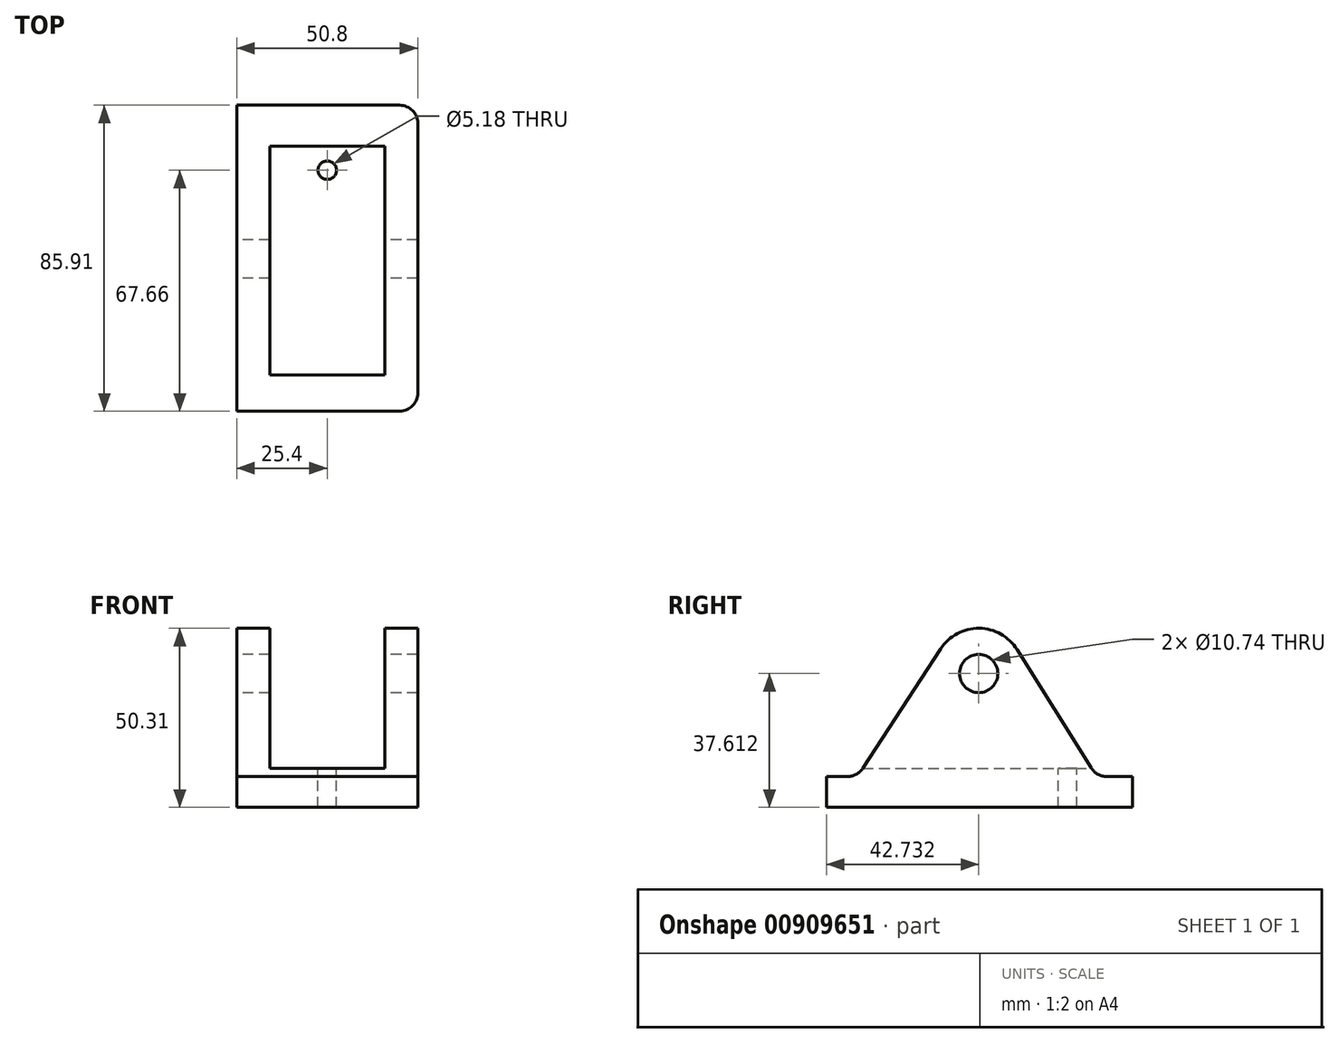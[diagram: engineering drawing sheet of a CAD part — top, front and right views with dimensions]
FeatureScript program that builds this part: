
annotation { "Feature Type Name" : "Feature", "Feature Type Description" : "" }
export const myFeature = defineFeature(function(context is Context, id is Id, definition is map)
    precondition{}
    {
        {
            var Q0;
            Q0=qCreatedBy(makeId("Right.planeOp"),FACE);
            var sketch = newSketch(context, id + "F0", { "sketchPlane" : qUnion([Q0])});
            skLineSegment(sketch, "E0.bottom", {"start": v(-40.85, -18.95) * mm, "end": v(45.06, -18.95) * mm});
            skLineSegment(sketch, "E0.top", {"start": v(-40.85, -27.65) * mm, "end": v(45.06, -27.65) * mm});
            skLineSegment(sketch, "E0.left", {"start": v(-40.85, -18.95) * mm, "end": v(-40.85, -27.65) * mm});
            skLineSegment(sketch, "E0.right", {"start": v(45.06, -18.95) * mm, "end": v(45.06, -27.65) * mm});
            skPoint(sketch, "E1.snap10", {"position": v(2.1, -18.95) * mm});
            skPoint(sketch, "E2.visualSharp", {"position": v(2.1, 33.55) * mm});
            skLineSegment(sketch, "E3", {"start": v(34.95, -18.95) * mm, "end": v(12.65, 16.7) * mm});
            skLineSegment(sketch, "E4", {"start": v(-8.75, 16.9) * mm, "end": v(-32.14, -18.95) * mm});
            skArc(sketch, "E5.filletArc", {"start": v(12.65, 16.7) * mm, "mid": v(2, 22.66) * mm, "end": v(-8.75, 16.9) * mm});
            skPoint(sketch, "E6", {"position": v(0, 0) * mm});
            skCircle(sketch, "E7", {"center": v(1.88, 9.96) * mm, "radius": 5.37 * mm});
            skSolve(sketch);
        }
        {
            var Q0;
            {var subQ0=sQuery(id+"F0.wireOp",EDGE,"E3");Q0=makeQuery(id+"F0.imprint","IMPRINT",FACE,{"disambiguationData":[TD([[makeQuery(id+"F0.imprint","IMPRINT",EDGE,{"derivedFrom":subQ0}),1.0]])]});}
            var Q1;
            Q1=makeQuery(id+"F0.imprint","IMPRINT",FACE,{"disambiguationData":[TD([[makeQuery(id+"F0.imprint","IMPRINT",EDGE,{"derivedFrom":sQuery(id+"F0.wireOp",EDGE,"E0.top")}),1.0]])]});
            extrude(context, id + "F1", {"entities" : qUnion([Q0, Q1]), "endBound" : BoundingType.SYMMETRIC, "depth" : 50.8 * mm, "offsetDistance" : 25.4 * mm});
        }
        {
            var Q0;
            Q0=makeQuery(id+"F1.opExtrude","CAP_EDGE",EDGE,{"disambiguationData":[OSD([sQuery(id+"F0.wireOp",EDGE,"E0.left")])],"isStart":false});
            var Q1;
            Q1=makeQuery(id+"F1.opExtrude","CAP_EDGE",EDGE,{"disambiguationData":[OSD([sQuery(id+"F0.wireOp",EDGE,"E0.right")])],"isStart":false});
            var Q2;
            Q2=makeQuery(id+"F1.opExtrude","SWEPT_EDGE",EDGE,{"disambiguationData":[OSD([sQuery(id+"F0.wireOp",EDGE,"E0.bottom"),sQuery(id+"F0.wireOp",EDGE,"E4")])]});
            var Q3;
            Q3=makeQuery(id+"F1.opExtrude","SWEPT_EDGE",EDGE,{"disambiguationData":[OSD([sQuery(id+"F0.wireOp",EDGE,"E0.bottom"),sQuery(id+"F0.wireOp",EDGE,"E3")])]});
            fillet(context, id + "F2", {"entities" : qUnion([Q0, Q1, Q2, Q3]), "radius" : 5.08 * mm, "tangentPropagation" : true, "allowEdgeOverflow" : false});
        }
        {
            var Q0;
            Q0=qCreatedBy(makeId("Front.planeOp"),FACE);
            var sketch = newSketch(context, id + "F3", { "sketchPlane" : qUnion([Q0])});
            skLineSegment(sketch, "E8", {"start": v(-16.14, 23.16) * mm, "end": v(-16.14, -16.7) * mm});
            skLineSegment(sketch, "E9.MirrorCS", {"start": v(16.14, 23.16) * mm, "end": v(16.14, -16.7) * mm});
            skLineSegment(sketch, "E10", {"start": v(-16.14, 23.16) * mm, "end": v(16.14, 23.16) * mm});
            skLineSegment(sketch, "E11", {"start": v(-16.14, -16.7) * mm, "end": v(16.14, -16.7) * mm});
            skSolve(sketch);
        }
        {
            var Q0;
            Q0 = qSketchRegion(id + "F3", true);
            extrude(context, id + "F4", {"entities" : qUnion([Q0]), "operationType" : NewBodyOperationType.REMOVE, "endBound" : BoundingType.THROUGH_ALL, "depth" : 25.4 * mm, "offsetDistance" : 25.4 * mm, "hasSecondDirection" : true, "secondDirectionOppositeDirection" : true, "secondDirectionDepth" : 50.8 * mm});
        }
        {
            var Q0;
            Q0=qCreatedBy(makeId("Top.planeOp"),FACE);
            var sketch = newSketch(context, id + "F5", { "sketchPlane" : qUnion([Q0])});
            skPoint(sketch, "E12", {"position": v(0, 26.81) * mm});
            skCircle(sketch, "E13", {"center": v(0, 26.81) * mm, "radius": 2.6 * mm});
            skSolve(sketch);
        }
        {
            var Q0;
            Q0=makeQuery(id+"F5.imprint","IMPRINT",FACE,{"disambiguationData":[TD([[makeQuery(id+"F5.imprint","IMPRINT",EDGE,{"derivedFrom":sQuery(id+"F5.wireOp",EDGE,"E13")}),1.0]])]});
            var Q1;
            Q1=sQuery(id+"F5.wireOp",EDGE,"E13");
            extrude(context, id + "F6", {"entities" : qUnion([Q0]), "operationType" : NewBodyOperationType.REMOVE, "surfaceOperationType" : NewSurfaceOperationType.ADD, "surfaceEntities" : qUnion([Q1]), "endBound" : BoundingType.THROUGH_ALL, "oppositeDirection" : true, "depth" : 25.4 * mm, "offsetDistance" : 25.4 * mm});
        }
    });
